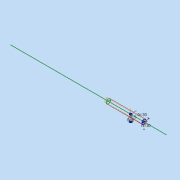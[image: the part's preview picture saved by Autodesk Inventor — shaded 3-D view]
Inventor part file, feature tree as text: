
AUTODESK INVENTOR PART (.ipt)
format: ipt  version: 2019 (Build 230136000, 136)  size: 106,496 bytes
history: native  units: mm
features: other x10, extrude x1, loft x1
ambient origin geometry x8: Origin, YZ Plane, XZ Plane, XY Plane, X Axis, Y Axis, Z Axis, Center Point
bodies: Body1 (feature_tree)
feature tree (12):
  other  "Твердое тело1"
  extrude  "Выдавливание1"  Depth=80.0mm TaperAngle=0.0deg
  other  "цилиндр_конец2"
  other  "РабОсь1"
  other  "РабПлоскость7"
  other  "РабПлоскость8"
  other  "ручка_конец1"
  other  "РабОсь2"
  loft  "Лофт1"
  other  "цилиндр_конец1"
  other  "РабПлоскость9"
  other  "ручка_конец2"
